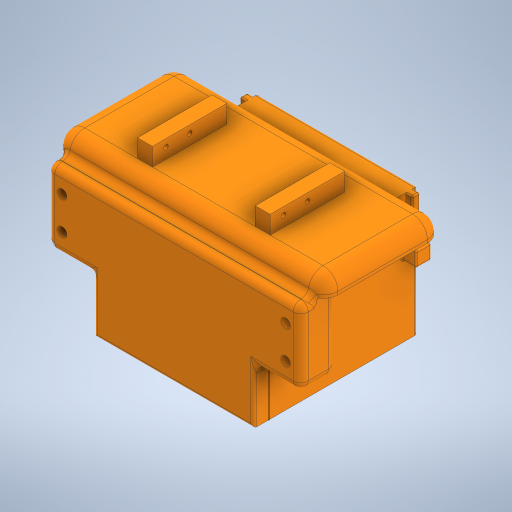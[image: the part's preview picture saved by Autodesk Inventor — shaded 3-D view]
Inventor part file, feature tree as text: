
AUTODESK INVENTOR PART (.ipt)
format: ipt  version: 2024.3 (Build 283343000, 343)  size: 673,280 bytes
history: native  units: mm
features: extrude x8, sketch x7, other x4, fillet x4
ambient origin geometry x8: Origin, YZ Plane, XZ Plane, XY Plane, X Axis, Y Axis, Z Axis, Center Point
bodies: Body1 (feature_tree)
feature tree (23):
  other  "Bryła1"
  sketch  "Szkic1"
  extrude  "Wyciągnięcie proste1"  Depth=93.0mm
  extrude  "Wyciągnięcie proste2"  Depth=72.0mm
  fillet  "Zaokrąglenie1"  Radius=107.0mm
  extrude  "Wyciągnięcie proste4"  Depth=86.0mm
  extrude  "Wyciągnięcie proste5"  Depth=10.0mm TaperAngle=0.0deg
  fillet  "Zaokrąglenie2"  Radius=100.0mm
  extrude  "Wyciągnięcie proste6"  Depth=2.0mm
  fillet  "Zaokrąglenie3"  Radius=5.0mm
  extrude  "Wyciągnięcie proste7"  Depth=5.0mm
  fillet  "Zaokrąglenie4"  Radius=92.0mm
  extrude  "Wyciągnięcie proste8"  Depth=53.0mm
  extrude  "Wyciągnięcie proste9"  Depth=28.0mm TaperAngle=0.0deg
  sketch  "Szkic3"
  sketch  "Szkic4"
  sketch  "Szkic6"
  sketch  "Szkic7"
  sketch  "Szkic8"
  sketch  "Szkic9"
  other  "Finish1"
  other  "Finish2"
  other  "Finish3"
